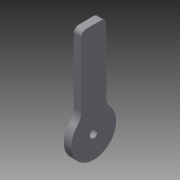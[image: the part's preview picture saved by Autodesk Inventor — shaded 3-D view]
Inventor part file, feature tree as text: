
AUTODESK INVENTOR PART (.ipt)
format: ipt  version: 2015 (Build 190159000, 159)  size: 94,720 bytes
history: native  units: mm
features: extrude x1, sketch x1
ambient origin geometry x8: Origin, YZ Plane, XZ Plane, XY Plane, X Axis, Y Axis, Z Axis, Center Point
bodies: Body1 (feature_tree)
feature tree (2):
  extrude  "Extrusion6"  Depth=3.0mm
  sketch  "Sketch1"  dims[d8=22.5deg d16=3.0mm d25=10.0mm d69=6.0mm d70=38.0mm d74=22.5deg d81=90.0mm d101=3.0mm d106=3.0mm d107=0.0mm d108=9.0mm d109=38.0mm d110=5.0mm d111=2.0mm]
